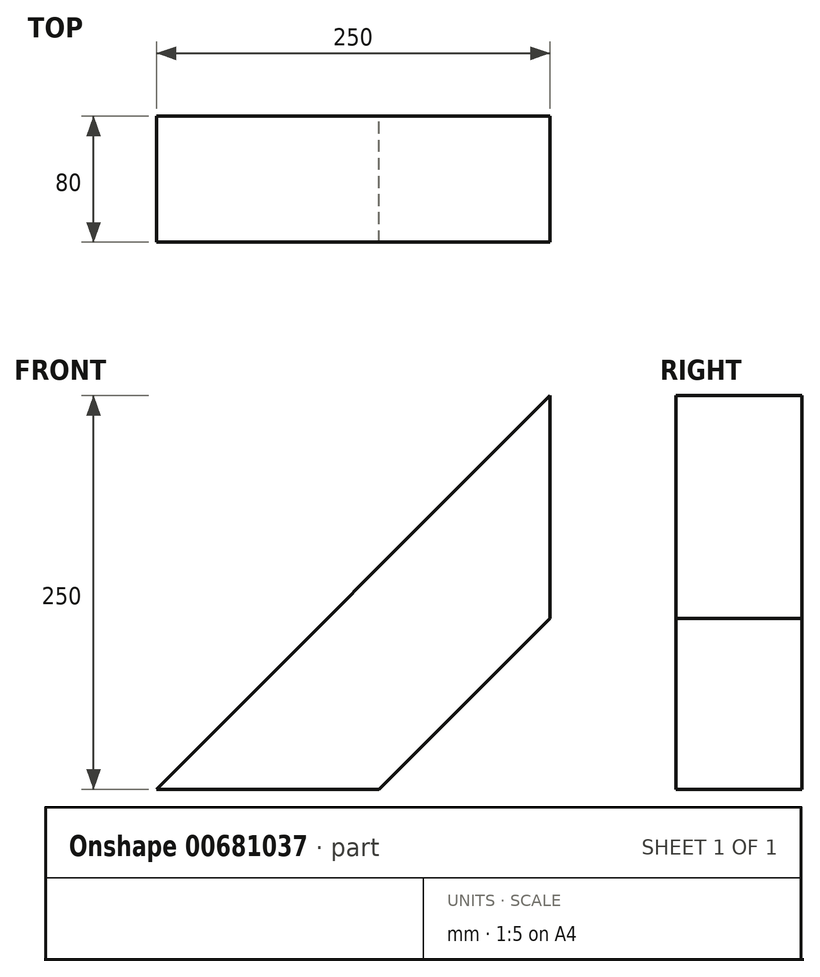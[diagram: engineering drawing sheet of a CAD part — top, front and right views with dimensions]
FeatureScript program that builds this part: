
annotation { "Feature Type Name" : "Feature", "Feature Type Description" : "" }
export const myFeature = defineFeature(function(context is Context, id is Id, definition is map)
    precondition{}
    {
        {
            var Q0;
            Q0=qCreatedBy(makeId("Front.planeOp"),FACE);
            var sketch = newSketch(context, id + "F0", { "sketchPlane" : qUnion([Q0])});
            skLineSegment(sketch, "E0", {"start": v(0, 0) * mm, "end": v(250, 250) * mm});
            skLineSegment(sketch, "E1", {"start": v(250, 250) * mm, "end": v(250, 108.58) * mm});
            skLineSegment(sketch, "E2", {"start": v(250, 108.58) * mm, "end": v(141.42, 0) * mm});
            skLineSegment(sketch, "E3", {"start": v(141.42, 0) * mm, "end": v(0, 0) * mm});
            skSolve(sketch);
        }
        {
            var Q0;
            Q0 = qSketchRegion(id + "F0", true);
            extrude(context, id + "F1", {"entities" : qUnion([Q0]), "depth" : 80 * mm, "offsetDistance" : 25 * mm});
        }
    });
